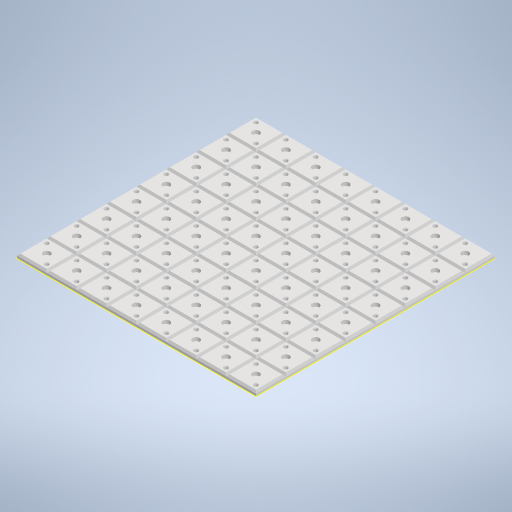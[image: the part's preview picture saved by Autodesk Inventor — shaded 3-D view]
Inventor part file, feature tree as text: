
AUTODESK INVENTOR PART (.ipt)
format: ipt  version: 2024.1 (Build 281209000, 209)  size: 662,016 bytes
history: native  units: in
note: dims shown in document units (in); Inventor stores cm internally (conversion verified against a paired STEP export)
features: sketch x5, extrude x4, chamfer x4, projected_geometry x2, pattern_linear x1
ambient origin geometry x8: Origin, YZ Plane, XZ Plane, XY Plane, X Axis, Y Axis, Z Axis, Center Point
bodies: Solid1 (feature_tree)
feature tree (16):
  extrude  "Extrusion1"  Depth=1.0039in
  chamfer  "Chamfer1"  Distance=0.1378in
  extrude  "Extrusion2"  Depth=0.0591in
  extrude  "Extrusion3"  Depth=1.0039in
  chamfer  "Chamfer2"  Distance=0.1181in
  pattern_linear  "Rectangular Pattern1"  Spacing1=0.1181in  [1 undecoded]
  sketch  "Sketch5"  dims[d11=0.502in d12=0.1181in d13=0.0in d14=0.1181in d15=0.1181in d16=0.1969in d17=0.1969in d18=0.1181in d19=0.0in d20=0.0197in d21=0.0787in d22=45.0deg d23=3.1496in d25=1.0039in d26=3.1496in d28=1.0039in d29=0.5118in d30=0.1378in d31=0.0in d32=0.0591in d33=0.0787in d34=45.0deg d35=0.0984in d36=0.0787in d37=45.0deg]
  extrude  "Extrusion4"  Depth=0.1181in
  chamfer  "Chamfer3"  Distance=0.1969in
  chamfer  "Chamfer4"  Distance=0.1969in
  sketch  "Sketch1"  dims[d0=1.0039in d1=1.0039in d2=0.1378in d3=0.0in]
  sketch  "Sketch2"  dims[d4=0.0591in d5=0.0787in d6=45.0deg d7=0.2362in]
  sketch  "Sketch3"  dims[d8=1.0039in d9=0.502in]
  sketch  "Sketch4"  dims[d10=1.0039in]
  projected_geometry  "Projected Loop1"
  projected_geometry  "Projected Loop2"
note: 1 required parameter value undecoded (feature->parameter linkage not recoverable at this tier; creation-order binding heuristic only, values carry confidence <= 0.55)
